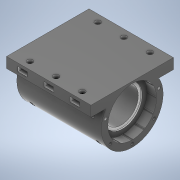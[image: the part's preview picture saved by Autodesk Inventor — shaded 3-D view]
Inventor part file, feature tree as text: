
AUTODESK INVENTOR PART (.ipt)
format: ipt  version: 2022 (Build 260153000, 153)  size: 547,840 bytes
history: native  units: mm
features: extrude x11, sketch x11, other x6, mirror x4, pattern_circular x2, fillet x1, projected_geometry x1
ambient origin geometry x8: Origin, YZ Plane, XZ Plane, XY Plane, X Axis, Y Axis, Z Axis, Center Point
bodies: Body1 (feature_tree)
feature tree (36):
  other  "Твердое тело1"
  extrude  "Выдавливание1"  Depth=26.0mm
  extrude  "Выдавливание2"  Depth=37.3mm
  extrude  "Выдавливание3"  Depth=50.0mm TaperAngle=0.0deg
  other  "РабПлоскость2"
  extrude  "Выдавливание4"  TaperAngle=0.0deg  [1 undecoded]
  other  "РабОсь1"
  pattern_circular  "Круговой массив1"  [2 undecoded]
  other  "РабПлоскость3"
  mirror  "Зеркальное отражение1"
  extrude  "Выдавливание5"  Depth=7.3mm TaperAngle=0.0deg
  extrude  "Выдавливание6"  Depth=2.1mm
  other  "РабПлоскость4"
  sketch  "Эскиз9"
  extrude  "Выдавливание9"  Depth=13.0mm TaperAngle=0.0deg
  fillet  "Сопряжение1"  [1 undecoded]
  pattern_circular  "Круговой массив2"  [2 undecoded]
  mirror  "Зеркальное отражение2"
  extrude  "Выдавливание10"  Depth=1.7mm TaperAngle=0.0deg
  mirror  "Зеркальное отражение3"
  other  "РабПлоскость5"
  extrude  "Выдавливание11"  Depth=50.0mm TaperAngle=210.0deg
  extrude  "Выдавливание12"  Depth=63.1mm
  mirror  "Зеркальное отражение4"
  extrude  "Выдавливание7"  Depth=8.0mm TaperAngle=0.0deg
  sketch  "Эскиз2"
  sketch  "Эскиз3"
  sketch  "Эскиз4"
  sketch  "Эскиз5"
  sketch  "Эскиз6"
  projected_geometry  "Спроецированная петля1"
  sketch  "Эскиз7"
  sketch  "Эскиз8"
  sketch  "Эскиз10"
  sketch  "Эскиз11"
  sketch  "Эскиз12"
note: 6 required parameter values undecoded (feature->parameter linkage not recoverable at this tier; creation-order binding heuristic only, values carry confidence <= 0.55)
